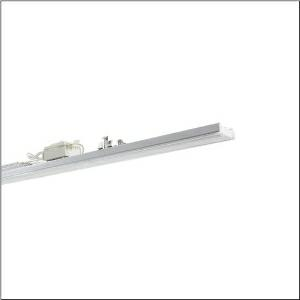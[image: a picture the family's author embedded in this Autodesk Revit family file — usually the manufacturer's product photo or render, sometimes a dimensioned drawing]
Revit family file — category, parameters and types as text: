
# Revit family: licross_r__21_recessed_mo_52tl12dv4dxgd_db2b
name_source: partatom
category: Lighting Fixtures
units: mm (PartAtom-declared; Revit-internal decimal feet)

## family parameters
Cut with Voids When Loaded = No
Host = Face
Light Source = No
Part Type = Normal
Room Calculation Point = No
Round Connector Dimension = Use Diameter
Shared = No

## types (1)
- --- (1 x LED, 13000 lm, 71 W, 4000K)
    Apparent Load = 71 VA
    CIE Flux Codes = 72 92 99 100 100
    Color Rendering = 80
    Color Temperature = 4000K
    Default Elevation = 1800 mm
    Description = Licross® 21 Recessed MO, luminaire insert, of sheet steel, galvanised, coil coated, white, length: 2.250mm, width: 66mm, height: 67mm, LED rated luminous flux: 13.000lm, light colour: 840, control gear: DALI 2 (for two DALI lines), with plug, 6-pole, with phase selection, mains connection: 220..240V, AC/DC, 0/50..60Hz, rated input power: 71W, internal wiring halogen-free, for central battery installations according to DIN EN 60598-2-22, for emergency light function, without changeover relay, primary optical cover: cover, of PMMA, light emission: direct distribution, primary light characteristic: symmetric, protection rating (complete): IP40, insulation class (complete): insulation class I (protective earthing), certification: CE, ENEC, VDE, UKCA, protection symbol: D if used in an environment without relevant dust loads with corresponding accessories, impact resistance: IK06, permissible ambient temperature for indoor applications: -25..+35°C, standard: EN 60598-2-22, corresponds to IFS (International Featured Standards) requirements for safety and quality in the food industry, reducing of maximum allowable ambient temperature of 5°C with ceiling mounting, LABS conformity tested according to VDMA 24364:2018-05, packaging unit: 1 piece
    Height = 58 mm
    Lamp = 1 x LED
    Lamp Light Flux = 13000 lm
    Lamp Power = 71 W
    Lamp count = 1
    Length = 2250 mm
    Luminous efficacy = 183 lm/W
    Manufacturer = Siteco
    ModVariant = No
    Model = 52TL12DV4DXGD
    Mounting Place = Ceiling
    Mounting Type = Pendant
    Number of Poles = 1
    OnlyDefault = Yes
    Power Factor = 1
    Product Name = Licross® 21 Recessed MO
    Product group = luminaire insert | ceiling pendant
    ProductGroupID = 902
    Protection Class = Protection class I
    Protection Degree = IP 40
    RLX_Detail_Level = 1
    RLX_Emergency_Light_Flux = 0 lm
    RLX_Emergency_Type = 0
    RLX_Emergency_Type_DB = No
    RlxData = <blob elided: 30185 chars, md5=0e876248>
    Socket = socket
    Standby Power = 0 W
    System Light Flux = 13000 lm
    System Power = 71 W
    Type Comments = : AC-mode, luminous flux: 100 % | dim-lin: 254 | 324 mA
    Type Image = l_1296930.jpg
    URL = http://relux.com
    VarID = @adj_134537
    Voltage = 0 V
    Weight = 0.00 kg
    Width = 66 mm

## geometry (parser evidence)
native form markers: Blend x4, Sweep x9
no freeform markers — native parametric forms only
